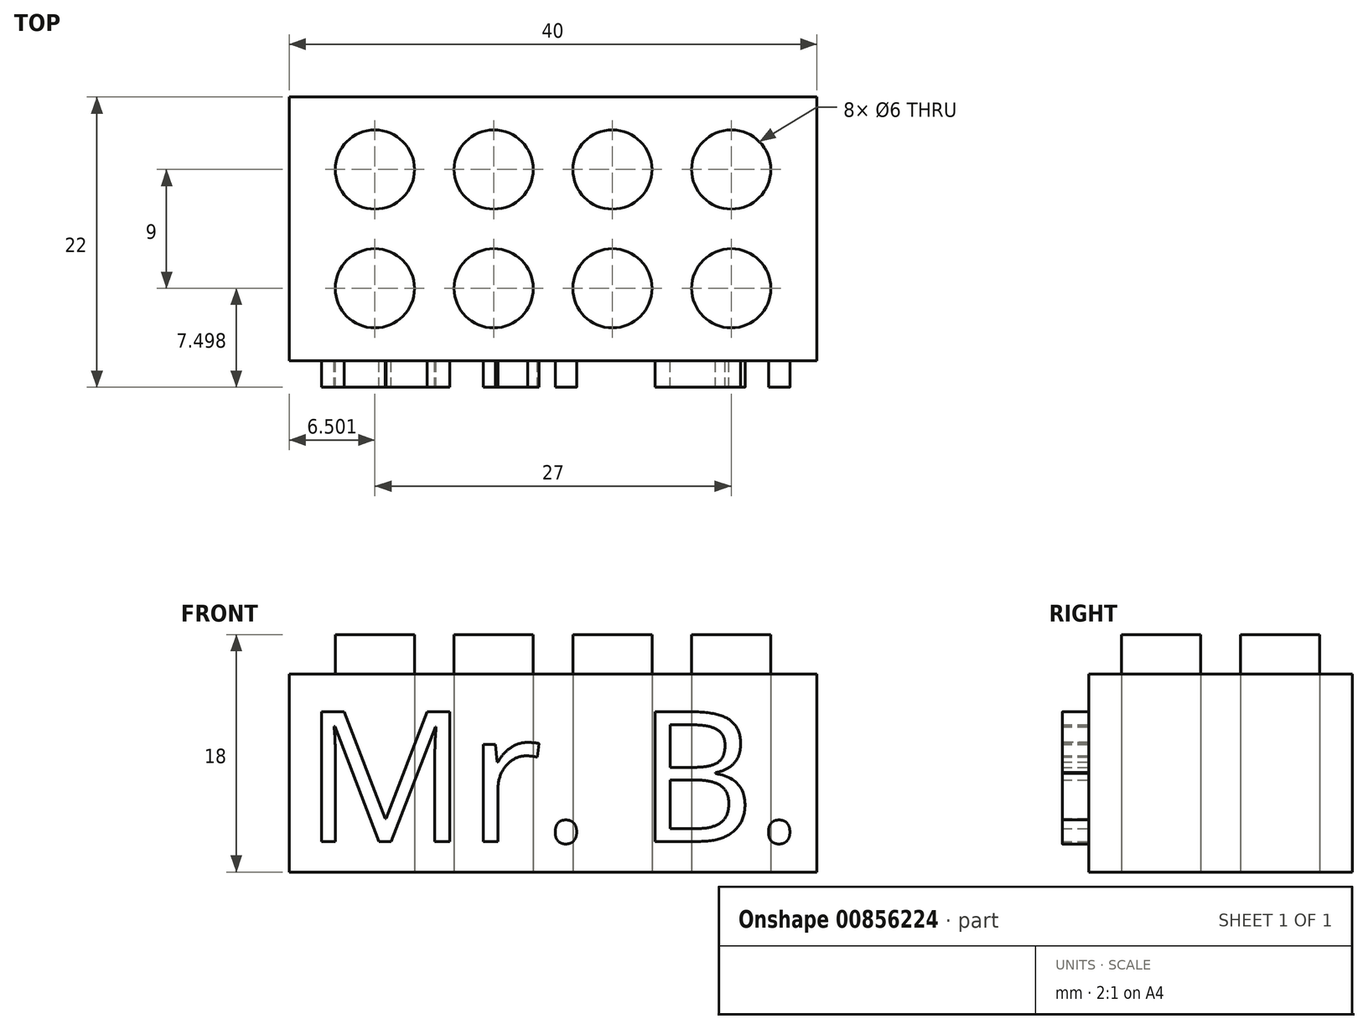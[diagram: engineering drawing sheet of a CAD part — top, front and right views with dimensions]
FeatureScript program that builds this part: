
annotation { "Feature Type Name" : "Feature", "Feature Type Description" : "" }
export const myFeature = defineFeature(function(context is Context, id is Id, definition is map)
    precondition{}
    {
        {
            var Q0;
            Q0=qCreatedBy(makeId("Top.planeOp"),FACE);
            var sketch = newSketch(context, id + "F0", { "sketchPlane" : qUnion([Q0])});
            skLineSegment(sketch, "E0.bottom", {"start": v(-14.25, 7) * mm, "end": v(25.75, 7) * mm});
            skLineSegment(sketch, "E0.top", {"start": v(-14.25, -13) * mm, "end": v(25.75, -13) * mm});
            skLineSegment(sketch, "E0.left", {"start": v(-14.25, 7) * mm, "end": v(-14.25, -13) * mm});
            skLineSegment(sketch, "E0.right", {"start": v(25.75, 7) * mm, "end": v(25.75, -13) * mm});
            skCircle(sketch, "E1", {"center": v(-7.75, -7.5) * mm, "radius": 3 * mm});
            skCircle(sketch, "E2", {"center": v(-7.75, 1.5) * mm, "radius": 3 * mm});
            skCircle(sketch, "E3", {"center": v(1.25, -7.5) * mm, "radius": 3 * mm});
            skCircle(sketch, "E4", {"center": v(10.25, -7.5) * mm, "radius": 3 * mm});
            skCircle(sketch, "E5", {"center": v(19.25, -7.5) * mm, "radius": 3 * mm});
            skCircle(sketch, "E6", {"center": v(1.25, 1.5) * mm, "radius": 3 * mm});
            skCircle(sketch, "E7", {"center": v(10.25, 1.5) * mm, "radius": 3 * mm});
            skCircle(sketch, "E8", {"center": v(19.25, 1.5) * mm, "radius": 3 * mm});
            skSolve(sketch);
        }
        {
            var Q0;
            Q0=makeQuery(id+"F0.imprint","IMPRINT",FACE,{"disambiguationData":[TD([[makeQuery(id+"F0.imprint","IMPRINT",EDGE,{"derivedFrom":sQuery(id+"F0.wireOp",EDGE,"E2")}),1.0]])]});
            var Q1;
            Q1=makeQuery(id+"F0.imprint","IMPRINT",FACE,{"disambiguationData":[TD([[makeQuery(id+"F0.imprint","IMPRINT",EDGE,{"derivedFrom":sQuery(id+"F0.wireOp",EDGE,"E3")}),1.0]])]});
            var Q2;
            Q2=makeQuery(id+"F0.imprint","IMPRINT",FACE,{"disambiguationData":[TD([[makeQuery(id+"F0.imprint","IMPRINT",EDGE,{"derivedFrom":sQuery(id+"F0.wireOp",EDGE,"E6")}),1.0]])]});
            var Q3;
            Q3=makeQuery(id+"F0.imprint","IMPRINT",FACE,{"disambiguationData":[TD([[makeQuery(id+"F0.imprint","IMPRINT",EDGE,{"derivedFrom":sQuery(id+"F0.wireOp",EDGE,"E4")}),1.0]])]});
            var Q4;
            Q4=makeQuery(id+"F0.imprint","IMPRINT",FACE,{"disambiguationData":[TD([[makeQuery(id+"F0.imprint","IMPRINT",EDGE,{"derivedFrom":sQuery(id+"F0.wireOp",EDGE,"E7")}),1.0]])]});
            var Q5;
            Q5=makeQuery(id+"F0.imprint","IMPRINT",FACE,{"disambiguationData":[TD([[makeQuery(id+"F0.imprint","IMPRINT",EDGE,{"derivedFrom":sQuery(id+"F0.wireOp",EDGE,"E5")}),1.0]])]});
            var Q6;
            Q6=makeQuery(id+"F0.imprint","IMPRINT",FACE,{"disambiguationData":[TD([[makeQuery(id+"F0.imprint","IMPRINT",EDGE,{"derivedFrom":sQuery(id+"F0.wireOp",EDGE,"E8")}),1.0]])]});
            var Q7;
            Q7=makeQuery(id+"F0.imprint","IMPRINT",FACE,{"disambiguationData":[TD([[makeQuery(id+"F0.imprint","IMPRINT",EDGE,{"derivedFrom":sQuery(id+"F0.wireOp",EDGE,"E1")}),1.0]])]});
            extrude(context, id + "F1", {"entities" : qUnion([Q0, Q1, Q2, Q3, Q4, Q5, Q6, Q7]), "depth" : 18 * mm, "offsetDistance" : 25 * mm});
        }
        {
            var Q0;
            Q0 = qSketchRegion(id + "F0", true);
            extrude(context, id + "F2", {"entities" : qUnion([Q0]), "depth" : 15 * mm, "offsetDistance" : 25 * mm});
        }
        {
            var Q0;
            Q0=makeQuery(id+"F2.opExtrude","SWEPT_FACE",FACE,{"disambiguationData":[OSD([sQuery(id+"F0.wireOp",EDGE,"E0.top")])]});
            var sketch = newSketch(context, id + "F3", { "sketchPlane" : qUnion([Q0])});
            skText(sketch, "E9", { "text": "Mr. B.", "fontName": "OpenSans-Regular.ttf"});
            const initialGuessF3  = {"E9": [-0.01315, 0.00232, 1, 0, 0.00991]};
            skSetInitialGuess(sketch, initialGuessF3);
            skSolve(sketch);
        }
        {
            var Q0;
            Q0 = qSketchRegion(id + "F3", true);
            extrude(context, id + "F4", {"entities" : qUnion([Q0]), "operationType" : NewBodyOperationType.ADD, "depth" : 2 * mm, "offsetDistance" : 25 * mm});
        }
    });
